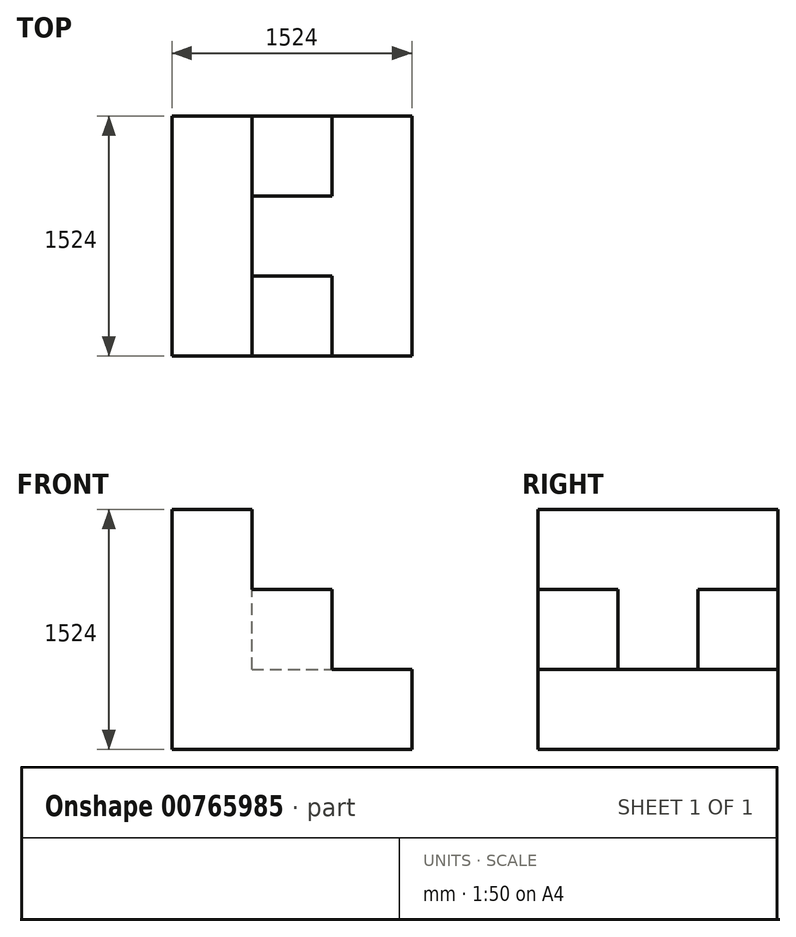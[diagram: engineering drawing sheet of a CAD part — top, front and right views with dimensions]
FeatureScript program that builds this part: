
annotation { "Feature Type Name" : "Feature", "Feature Type Description" : "" }
export const myFeature = defineFeature(function(context is Context, id is Id, definition is map)
    precondition{}
    {
        {
            var Q0;
            Q0=qCreatedBy(makeId("Front.planeOp"),FACE);
            var sketch = newSketch(context, id + "F0", { "sketchPlane" : qUnion([Q0])});
            skLineSegment(sketch, "E0.bottom", {"start": v(0, 0) * mm, "end": v(1524, 0) * mm});
            skLineSegment(sketch, "E0.top", {"start": v(0, 1524) * mm, "end": v(1524, 1524) * mm});
            skLineSegment(sketch, "E0.left", {"start": v(0, 0) * mm, "end": v(0, 1524) * mm});
            skLineSegment(sketch, "E0.right", {"start": v(1524, 0) * mm, "end": v(1524, 1524) * mm});
            skSolve(sketch);
        }
        {
            var Q0;
            Q0=makeQuery(id+"F0.imprint","IMPRINT",FACE,{"disambiguationData":[TD([[makeQuery(id+"F0.imprint","IMPRINT",EDGE,{"derivedFrom":sQuery(id+"F0.wireOp",EDGE,"E0.bottom")}),1.0]])]});
            extrude(context, id + "F1", {"entities" : qUnion([Q0]), "depth" : 1524 * mm, "offsetDistance" : 25.4 * mm});
        }
        {
            var Q0;
            Q0=makeQuery(id+"F1.opExtrude","CAP_FACE",FACE,{"disambiguationData":[OSD([sQuery(id+"F0.wireOp",EDGE,"E0.bottom"),sQuery(id+"F0.wireOp",EDGE,"E0.top"),sQuery(id+"F0.wireOp",EDGE,"E0.left"),sQuery(id+"F0.wireOp",EDGE,"E0.right")])],"isStart":false});
            var sketch = newSketch(context, id + "F2", { "sketchPlane" : qUnion([Q0])});
            skLineSegment(sketch, "E1", {"start": v(0, 1524) * mm, "end": v(508, 1524) * mm});
            skLineSegment(sketch, "E2", {"start": v(508, 1524) * mm, "end": v(508, 1016) * mm});
            skLineSegment(sketch, "E3", {"start": v(508, 1016) * mm, "end": v(1016, 1016) * mm});
            skLineSegment(sketch, "E4", {"start": v(1016, 1016) * mm, "end": v(1016, 508) * mm});
            skLineSegment(sketch, "E5", {"start": v(1016, 508) * mm, "end": v(1524, 508) * mm});
            skSolve(sketch);
        }
        {
            var Q0;
            {var subQ1=sQuery(id+"F2.wireOp",EDGE,"E2");Q0=makeQuery(id+"F2.imprint","IMPRINT",FACE,{"disambiguationData":[TD([[makeQuery(id+"F2.imprint","IMPRINT",EDGE,{"derivedFrom":subQ1}),1.0]])]});}
            extrude(context, id + "F3", {"entities" : qUnion([Q0]), "operationType" : NewBodyOperationType.REMOVE, "oppositeDirection" : true, "depth" : 1524 * mm, "offsetDistance" : 25.4 * mm});
        }
        {
            var Q0;
            Q0=makeQuery(id+"F3.boolean.opBoolean","COPY",FACE,{"derivedFrom":makeQuery(id+"F3.opExtrude","SWEPT_FACE",FACE,{"disambiguationData":[OSD([sQuery(id+"F2.wireOp",EDGE,"E4")])]})});
            var sketch = newSketch(context, id + "F4", { "sketchPlane" : qUnion([Q0])});
            skLineSegment(sketch, "E6", {"start": v(-1524, 508) * mm, "end": v(-1016, 508) * mm});
            skLineSegment(sketch, "E7", {"start": v(-1016, 508) * mm, "end": v(-1016, 1016) * mm});
            skLineSegment(sketch, "E8", {"start": v(-1016, 1016) * mm, "end": v(-508, 1016) * mm});
            skLineSegment(sketch, "E9", {"start": v(-508, 1016) * mm, "end": v(-508, 508) * mm});
            skLineSegment(sketch, "E10", {"start": v(-508, 508) * mm, "end": v(0, 508) * mm});
            skLineSegment(sketch, "E11", {"start": v(-1016, 508) * mm, "end": v(-508, 508) * mm});
            skSolve(sketch);
        }
        {
            var Q0;
            Q0=makeQuery(id+"F4.imprint","IMPRINT",FACE,{"disambiguationData":[TD([[makeQuery(id+"F4.imprint","IMPRINT",EDGE,{"derivedFrom":sQuery(id+"F4.wireOp",EDGE,"E7")}),-1.0]])]});
            extrude(context, id + "F5", {"entities" : qUnion([Q0]), "operationType" : NewBodyOperationType.REMOVE, "oppositeDirection" : true, "depth" : 508 * mm, "offsetDistance" : 25.4 * mm});
        }
    });
